# Revit family: Gira_041430
name_source: partatom
category: Electrical Fixtures
revit_build: Autodesk Revit 2017 (Build: 20160225_1515(x64)
units: mm (PartAtom-declared; Revit-internal decimal feet)

## family parameters
Cut with Voids When Loaded = No
Host = Face
Maintain Annotation Orientation = Yes
Part Type = Normal
Room Calculation Point = No
Round Connector Dimension = Use Diameter
Shared = No

## types (1)
- SCHUKO HC + SH WP surface-mounted grey
    Antibacterial treatment = No
    Available = No
    BIM (1) = https://media.stage.bim.site
    Category = Socket outlet
    Colour = Grey
    Connection type = Plug clamp
    Data sheet (1) = https://katalog.gira.de
    Default Elevation = 1219 mm
    Description = SCHUKO HC SH WP SM GY,SCHUKO socket outlet 16 A 250 V~ hinged cover, integrated increased contact protection (shutter) and symbol ,,grey,Notes :,- Increased contact protection pursuant to DIN-VDE 0620-1.
    Eject-mechanism = No
    Fault current protection = No
    Für "erschwerte Bedingungen" (nach VDE) (*de-DE) = No
    GTIN = 4010337017387
    HAN = 041430
    Halogen free = No
    HeinzeBIM = https://bimportal.heinze.de
    Imprint/indication = Without imprint
    Insulated mounting = No
    Label space/information surface = No
    Lockable = No
    Manufacturer = Gira
    Manufacturer URL = https://www.gira.de
    Material = Other
    Material quality = Other
    Model = Protective contact (SCHUKO)
    Mounting method = Surface mounted (plaster)
    Name = SCHUKO HC + SH WP surface-mounted grey
    Nominal current = 16
    Nominal voltage = 250
    Number of modules (module system) = 1
    Number of socket outlets switchable = 0
    Number of units = 1
    Over voltage protection = No
    Protective earth pin round = No
    Rotated central insert = No
    Special power supply = No special power supply
    Suitable for degree of protection (IP) = IP44
    Surface protection = Other
    Transparent = No
    Type of fastening = Mounting with screw
    URL = http://katalog.gira.de
    With built-in USB power supply = No
    With child-protection = Yes
    With function lighting = No
    With hinged lid = Yes
    With loop through function = No
    With miniature fuse = No
    With on/off switch = No
    With orientation lighting = No
    With signal lamp = No

## geometry (parser evidence)
native form markers: Sweep x3
no freeform markers — native parametric forms only
